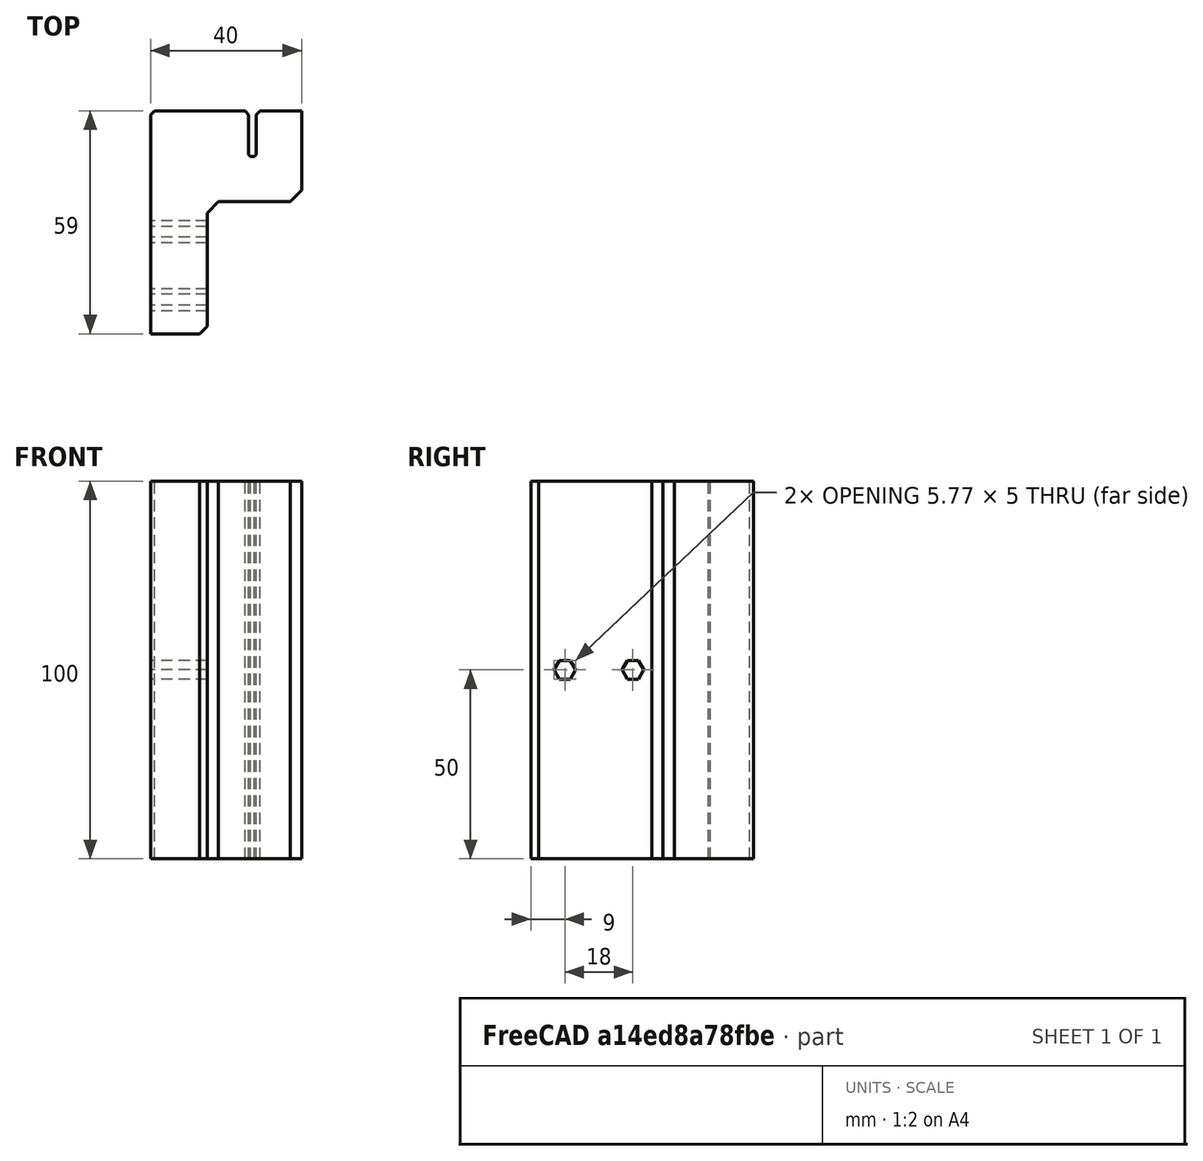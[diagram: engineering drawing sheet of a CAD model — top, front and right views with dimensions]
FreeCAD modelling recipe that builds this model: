
FCSTD DOCUMENT  (FreeCAD 0.19R)
Label: TankClip
License: All rights reserved
LicenseURL: http://en.wikipedia.org/wiki/All_rights_reserved
objects: PartDesign::Chamfer×8, Sketcher::SketchObject×2, PartDesign::Pad×1, PartDesign::Pocket×1, PartDesign::Body×1, Mesh::Feature×1
note: 23 computed .brp shape members not serialized (recipe doc carries the construction recipe); baked Part::Feature solids carry a one-line shape summary decoded from their .brp

FEATURE [Sketcher::SketchObject] Sketch
  FullyConstrained = false
  MapMode = 5
  Support = -> [XY_Plane]
  sketch-geometry (10):
    g0: LineSegment StartX=0 StartY=0 StartZ=0 EndX=0 EndY=-59 EndZ=0
    g1: LineSegment StartX=0 StartY=-59 StartZ=0 EndX=15 EndY=-59 EndZ=0
    g2: LineSegment StartX=15 StartY=-59 StartZ=0 EndX=15 EndY=-24 EndZ=0
    g3: LineSegment StartX=15 StartY=-24 StartZ=0 EndX=40 EndY=-24 EndZ=0
    g4: LineSegment StartX=40 StartY=-24 StartZ=0 EndX=40 EndY=0 EndZ=0
    g5: LineSegment StartX=26 StartY=0 StartZ=0 EndX=26 EndY=-12 EndZ=0
    g6: LineSegment StartX=26 StartY=-12 StartZ=0 EndX=28 EndY=-12 EndZ=0
    g7: LineSegment StartX=28 StartY=-12 StartZ=0 EndX=28 EndY=0 EndZ=0
    g8: LineSegment StartX=0 StartY=0 StartZ=0 EndX=26 EndY=0 EndZ=0
    g9: LineSegment StartX=28 StartY=0 StartZ=0 EndX=40 EndY=0 EndZ=0
  constraints (27):
    c: Coincident(g-1,g0)
    c: PointOnObject(g0,g-2)
    c: Coincident(g0,g1)
    c: Horizontal(g1)
    c: Coincident(g1,g2)
    c: Vertical(g2)
    c: Coincident(g2,g3)
    c: Coincident(g3,g4)
    c: PointOnObject(g4,g-1)
    c: Vertical(g4)
    c: PointOnObject(g5,g-1)
    c: Vertical(g5)
    c: Coincident(g5,g6)
    c: Coincident(g6,g7)
    c: PointOnObject(g7,g-1)
    c: Vertical(g7)
    c: Horizontal(g6)
    c: Distance(g6) = 2
    c: Distance(g5) = 12
    c: Distance(g1) = 15
    c: Distance(g6,g3) = 12
    c: Horizontal(g3)
    c: Distance(g2) = 35
    c: Coincident(g0,g8)
    c: Coincident(g8,g5)
    c: Coincident(g7,g9)
    c: Coincident(g9,g4)
FEATURE [PartDesign::Pad] Pad
  Direction = (1,1,1)
  Length = 100
  Length2 = 100
  Profile = -> Sketch
  Type = 0
FEATURE [Sketcher::SketchObject] Sketch001
  FullyConstrained = true
  MapMode = 5
  Placement = pos=(15,0,0) rot=(0.57735,0.57735,0.57735;2.0944rad)
  Support = -> [Pad]
  sketch-geometry (14):
    g0: LineSegment StartX=-48.5566 StartY=47.5 StartZ=0 EndX=-47.1132 EndY=50 EndZ=0
    g1: LineSegment StartX=-47.1132 StartY=50 StartZ=0 EndX=-48.5566 EndY=52.5 EndZ=0
    g2: LineSegment StartX=-48.5566 StartY=52.5 StartZ=0 EndX=-51.4434 EndY=52.5 EndZ=0
    g3: LineSegment StartX=-51.4434 StartY=52.5 StartZ=0 EndX=-52.8868 EndY=50 EndZ=0
    g4: LineSegment StartX=-52.8868 StartY=50 StartZ=0 EndX=-51.4434 EndY=47.5 EndZ=0
    g5: LineSegment StartX=-51.4434 StartY=47.5 StartZ=0 EndX=-48.5566 EndY=47.5 EndZ=0
    g6: Circle CenterX=-50 CenterY=50 CenterZ=0 NormalX=0 NormalY=0 NormalZ=1 AngleXU=0 Radius=2.88675
    g7: LineSegment StartX=-30.5566 StartY=47.5 StartZ=0 EndX=-29.1132 EndY=50 EndZ=0
    g8: LineSegment StartX=-29.1132 StartY=50 StartZ=0 EndX=-30.5566 EndY=52.5 EndZ=0
    g9: LineSegment StartX=-30.5566 StartY=52.5 StartZ=0 EndX=-33.4434 EndY=52.5 EndZ=0
    g10: LineSegment StartX=-33.4434 StartY=52.5 StartZ=0 EndX=-34.8868 EndY=50 EndZ=0
    g11: LineSegment StartX=-34.8868 StartY=50 StartZ=0 EndX=-33.4434 EndY=47.5 EndZ=0
    g12: LineSegment StartX=-33.4434 StartY=47.5 StartZ=0 EndX=-30.5566 EndY=47.5 EndZ=0
    g13: Circle CenterX=-32 CenterY=50 CenterZ=0 NormalX=0 NormalY=0 NormalZ=1 AngleXU=0 Radius=2.88675
  constraints (34):
    c: Coincident(g0,g1)
    c: Coincident(g1,g2)
    c: Coincident(g2,g3)
    c: Coincident(g3,g4)
    c: Coincident(g4,g5)
    c: Coincident(g5,g0)
    c: Equal(g0, g1-g5) x5
    c: PointOnObject(g0,g6)
    c: PointOnObject(g1,g6)
    c: PointOnObject(g2,g6)
    c: PointOnObject(g3,g6)
    c: PointOnObject(g4,g6)
    c: PointOnObject(g5,g6)
    c: Coincident(g7,g8)
    c: Coincident(g8,g9)
    c: Coincident(g9,g10)
    c: Coincident(g10,g11)
    c: Coincident(g11,g12)
    c: Coincident(g12,g7)
    c: Equal(g7, g8-g12) x5
    c: PointOnObject(g7,g13)
    c: PointOnObject(g8,g13)
    c: PointOnObject(g9,g13)
    c: PointOnObject(g10,g13)
    c: PointOnObject(g11,g13)
    c: PointOnObject(g12,g13)
    c: Horizontal(g9)
    c: Horizontal(g2)
    c: Distance(g1,g3) = 5
    c: Distance(g8,g10) = 5
    c: DistanceY(g13) = 50
    c: DistanceY(g6) = 50
    c: DistanceX(g13) = -32
    c: Distance(g6,g13) = 18
FEATURE [PartDesign::Pocket] Pocket
  BaseFeature = -> Pad
  Length = 5
  Length2 = 100
  Profile = -> Sketch001
  Type = 1
FEATURE [PartDesign::Chamfer] Chamfer
  Angle = 45
  Base = -> Pocket [Edge63]
  BaseFeature = -> Pocket
  ChamferType = 0
  FlipDirection = false
  Size = 3
  Size2 = 1
  SupportTransform = false
FEATURE [PartDesign::Chamfer] Chamfer001
  Angle = 45
  Base = -> Chamfer [Edge31]
  BaseFeature = -> Chamfer
  ChamferType = 0
  FlipDirection = false
  Size = 3
  Size2 = 1
  SupportTransform = false
FEATURE [PartDesign::Chamfer] Chamfer002
  Angle = 45
  Base = -> Chamfer001 [Edge56]
  BaseFeature = -> Chamfer001
  ChamferType = 0
  FlipDirection = false
  Size = 0.5
  Size2 = 1
  SupportTransform = false
FEATURE [PartDesign::Chamfer] Chamfer003
  Angle = 45
  Base = -> Chamfer002 [Edge15]
  BaseFeature = -> Chamfer002
  ChamferType = 0
  FlipDirection = false
  Size = 0.5
  Size2 = 1
  SupportTransform = false
FEATURE [PartDesign::Chamfer] Chamfer004
  Angle = 45
  Base = -> Chamfer003 [Edge22]
  BaseFeature = -> Chamfer003
  ChamferType = 0
  FlipDirection = false
  Size = 1
  Size2 = 1
  SupportTransform = false
FEATURE [PartDesign::Chamfer] Chamfer005
  Angle = 45
  Base = -> Chamfer004 [Edge33]
  BaseFeature = -> Chamfer004
  ChamferType = 0
  FlipDirection = false
  Size = 1
  Size2 = 1
  SupportTransform = false
FEATURE [PartDesign::Chamfer] Chamfer006
  Angle = 45
  Base = -> Chamfer005 [Edge24]
  BaseFeature = -> Chamfer005
  ChamferType = 0
  FlipDirection = false
  Size = 1
  Size2 = 1
  SupportTransform = false
FEATURE [PartDesign::Chamfer] Chamfer007
  Angle = 45
  Base = -> Chamfer006 [Edge41]
  BaseFeature = -> Chamfer006
  ChamferType = 0
  FlipDirection = false
  Size = 2
  Size2 = 1
  SupportTransform = false
FEATURE [PartDesign::Body] Body
  Group = -> [Sketch,Pad,Sketch001,Pocket,Chamfer,Chamfer001,Chamfer002,Chamfer003,Chamfer004,Chamfer005,Chamfer006,Chamfer007]
  Origin = -> Origin
  Tip = -> Chamfer007
FEATURE [Mesh::Feature] Mesh  label="Chamfer007 (Meshed)"
